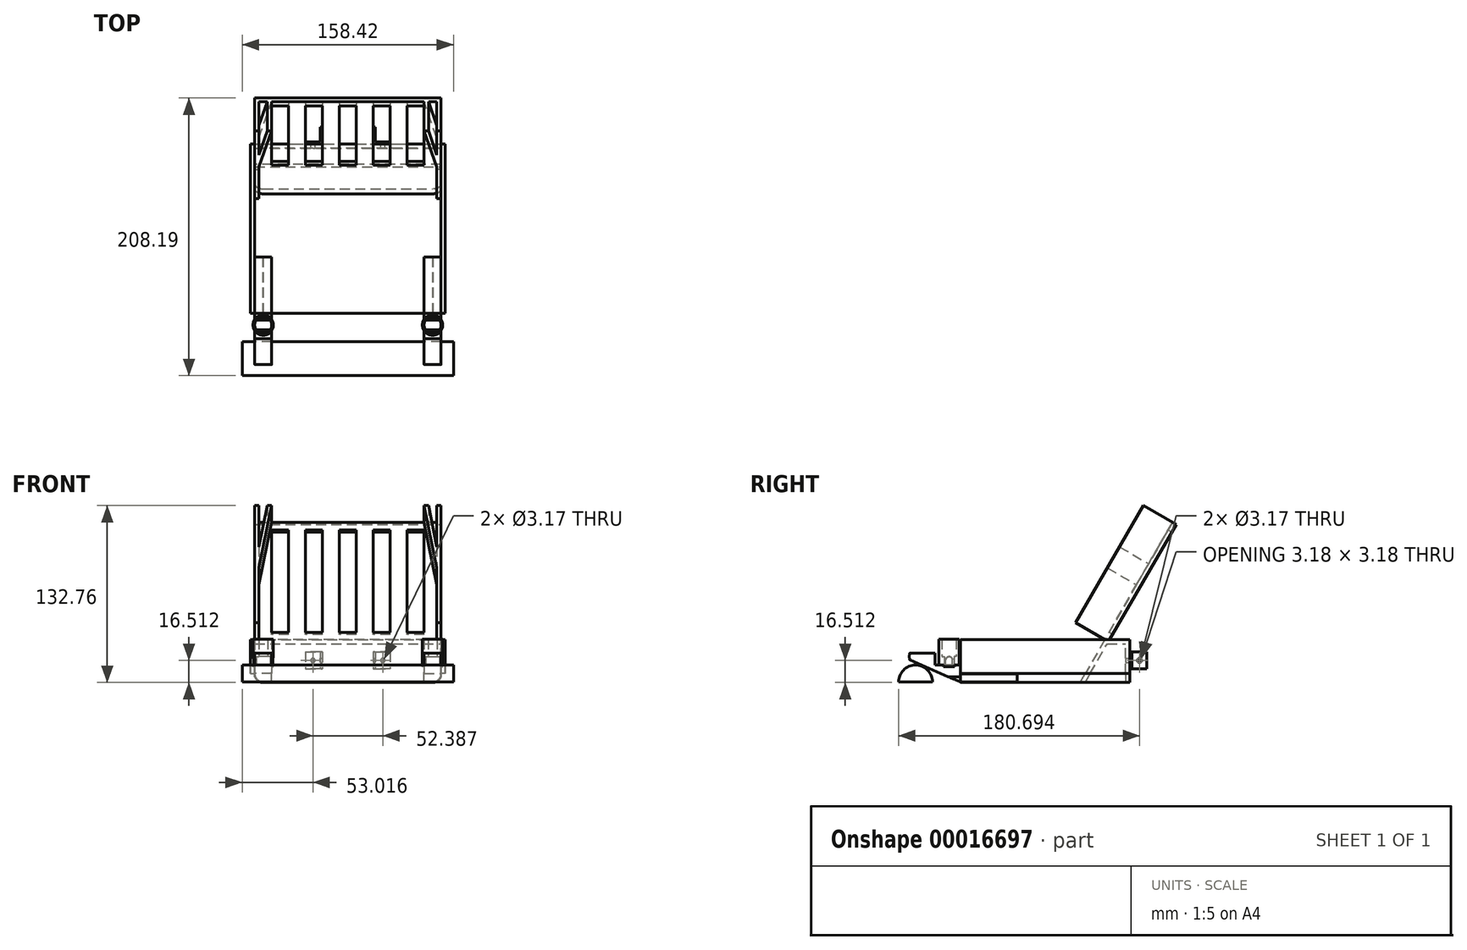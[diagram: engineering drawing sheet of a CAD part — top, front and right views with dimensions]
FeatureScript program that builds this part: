
annotation { "Feature Type Name" : "Feature", "Feature Type Description" : "" }
export const myFeature = defineFeature(function(context is Context, id is Id, definition is map)
    precondition{}
    {
        {
            var Q0;
            Q0=qCreatedBy(makeId("Front.planeOp"),FACE);
            var sketch = newSketch(context, id + "F0", { "sketchPlane" : qUnion([Q0])});
            skLineSegment(sketch, "E0.top", {"start": v(-63.5, 0) * mm, "end": v(63.5, 0) * mm});
            skLineSegment(sketch, "E0.left", {"start": v(-69.85, 31.75) * mm, "end": v(-69.85, 6.35) * mm});
            skLineSegment(sketch, "E0.right", {"start": v(69.85, 31.75) * mm, "end": v(69.85, 6.35) * mm});
            skLineSegment(sketch, "E1.0", {"start": v(70.17, 31.75) * mm, "end": v(70.17, 6.03) * mm});
            skLineSegment(sketch, "E1.1", {"start": v(-63.82, -0.32) * mm, "end": v(63.82, -0.32) * mm});
            skLineSegment(sketch, "E1.2", {"start": v(-70.17, 31.75) * mm, "end": v(-70.17, 6.03) * mm});
            skLineSegment(sketch, "E2", {"start": v(-70.17, 31.75) * mm, "end": v(-69.85, 31.75) * mm});
            skLineSegment(sketch, "E3", {"start": v(69.85, 31.75) * mm, "end": v(70.17, 31.75) * mm});
            skPoint(sketch, "E4.visualSharp", {"position": v(-70.17, -0.32) * mm});
            skArc(sketch, "E4.filletArc", {"start": v(-70.17, 6.03) * mm, "mid": v(-68.3, 1.54) * mm, "end": v(-63.82, -0.32) * mm});
            skPoint(sketch, "E5.visualSharp", {"position": v(-69.85, 0) * mm});
            skArc(sketch, "E5.filletArc", {"start": v(-69.85, 6.35) * mm, "mid": v(-68, 1.86) * mm, "end": v(-63.5, 0) * mm});
            skPoint(sketch, "E6.visualSharp", {"position": v(70.17, -0.32) * mm});
            skArc(sketch, "E6.filletArc", {"start": v(63.82, -0.32) * mm, "mid": v(68.3, 1.54) * mm, "end": v(70.17, 6.03) * mm});
            skPoint(sketch, "E7.visualSharp", {"position": v(69.85, 0) * mm});
            skArc(sketch, "E7.filletArc", {"start": v(63.5, 0) * mm, "mid": v(68, 1.86) * mm, "end": v(69.85, 6.35) * mm});
            skLineSegment(sketch, "E8.bottom", {"start": v(-70.17, 31.75) * mm, "end": v(-73.01, 31.75) * mm});
            skLineSegment(sketch, "E8.top", {"start": v(-70.17, 6.35) * mm, "end": v(-73.01, 6.35) * mm});
            skLineSegment(sketch, "E8.left", {"start": v(-70.17, 31.75) * mm, "end": v(-70.17, 6.35) * mm});
            skLineSegment(sketch, "E8.right", {"start": v(-73.01, 31.75) * mm, "end": v(-73.01, 6.35) * mm});
            skLineSegment(sketch, "E9", {"start": v(0, 0) * mm, "end": v(0, 50.9) * mm, "construction": true});
            skLineSegment(sketch, "E10.0.MirrorCS", {"start": v(70.17, 31.75) * mm, "end": v(73.01, 31.75) * mm});
            skLineSegment(sketch, "E11.0.MirrorCS", {"start": v(73.01, 31.75) * mm, "end": v(73.01, 6.35) * mm});
            skLineSegment(sketch, "E12.0.MirrorCS", {"start": v(70.17, 6.35) * mm, "end": v(73.01, 6.35) * mm});
            skSolve(sketch);
        }
        {
            var Q0;
            Q0=makeQuery(id+"F0.imprint","IMPRINT",FACE,{"disambiguationData":[TD([[makeQuery(id+"F0.imprint","IMPRINT",EDGE,{"derivedFrom":sQuery(id+"F0.wireOp",EDGE,"E0.top")}),-1.0]])]});
            extrude(context, id + "F1", {"entities" : qUnion([Q0]), "oppositeDirection" : true, "depth" : 127 * mm});
        }
        {
            var Q0;
            Q0=makeQuery(id+"F0.imprint","IMPRINT",FACE,{"disambiguationData":[TD([[makeQuery(id+"F0.imprint","IMPRINT",EDGE,{"derivedFrom":sQuery(id+"F0.wireOp",EDGE,"E8.bottom")}),1.0]])]});
            var Q1;
            {var subQ0=sQuery(id+"F0.wireOp",EDGE,"E10.0.MirrorCS");Q1=makeQuery(id+"F0.imprint","IMPRINT",FACE,{"disambiguationData":[TD([[makeQuery(id+"F0.imprint","IMPRINT",EDGE,{"derivedFrom":subQ0}),-1.0]])]});}
            var Q2;
            Q2=sQuery(id+"F0.wireOp",EDGE,"E8.right");
            var Q3;
            {var subQ0=sQuery(id+"F3.wireOp",EDGE,"E20.right");Q3=makeQuery(id+"F5.boolean.opBoolean","MERGE",FACE,{"derivedFrom":[makeQuery(id+"F4.boolean.opBoolean","MERGE",FACE,{"derivedFrom":[makeQuery(id+"F1.opExtrude","CAP_FACE",FACE,{"disambiguationData":[OSD([sQuery(id+"F0.wireOp",EDGE,"E0.top"),sQuery(id+"F0.wireOp",EDGE,"E0.left"),sQuery(id+"F0.wireOp",EDGE,"E0.right"),sQuery(id+"F0.wireOp",EDGE,"E1.0"),sQuery(id+"F0.wireOp",EDGE,"E1.1"),sQuery(id+"F0.wireOp",EDGE,"E1.2"),sQuery(id+"F0.wireOp",EDGE,"E2"),sQuery(id+"F0.wireOp",EDGE,"E3"),sQuery(id+"F0.wireOp",EDGE,"E4.filletArc"),sQuery(id+"F0.wireOp",EDGE,"E5.filletArc"),sQuery(id+"F0.wireOp",EDGE,"E6.filletArc"),sQuery(id+"F0.wireOp",EDGE,"E7.filletArc"),sQuery(id+"F0.wireOp",EDGE,"E8.left")])],"isStart":false}),makeQuery(id+"F4.opExtrude","SWEPT_FACE",FACE,{"disambiguationData":[OSD([subQ0])]})]}),makeQuery(id+"F5.opExtrude","SWEPT_FACE",FACE,{"disambiguationData":[OSD([subQ0])]})]});}
            extrude(context, id + "F2", {"entities" : qUnion([Q0, Q1]), "operationType" : NewBodyOperationType.ADD, "surfaceEntities" : qUnion([Q2]), "endBound" : BoundingType.UP_TO_SURFACE, "oppositeDirection" : true, "endBoundEntityFace" : qUnion([Q3]), "depth" : 25.4 * mm});
        }
        {
            var Q0;
            Q0=qCreatedBy(makeId("Right.planeOp"),FACE);
            var sketch = newSketch(context, id + "F3", { "sketchPlane" : qUnion([Q0])});
            skLineSegment(sketch, "E13", {"start": v(123.83, 31.75) * mm, "end": v(125.31, 31.75) * mm});
            skLineSegment(sketch, "E14", {"start": v(111.76, 31.75) * mm, "end": v(93.43, 0) * mm});
            skLineSegment(sketch, "E15", {"start": v(93.43, 0) * mm, "end": v(89.76, 0) * mm});
            skLineSegment(sketch, "E16", {"start": v(89.76, 0) * mm, "end": v(108.1, 31.75) * mm});
            skLineSegment(sketch, "E17", {"start": v(108.1, 31.75) * mm, "end": v(109.93, 31.75) * mm});
            skLineSegment(sketch, "E18.0", {"start": v(127, 6.35) * mm, "end": v(127, 6.03) * mm});
            skLineSegment(sketch, "E19.0", {"start": v(127, -0.32) * mm, "end": v(127, 6.03) * mm});
            skLineSegment(sketch, "E20.bottom", {"start": v(123.83, 31.75) * mm, "end": v(127, 31.75) * mm});
            skLineSegment(sketch, "E20.top", {"start": v(123.83, -0.32) * mm, "end": v(127, -0.32) * mm});
            skLineSegment(sketch, "E20.left", {"start": v(123.83, 31.75) * mm, "end": v(123.83, -0.32) * mm});
            skLineSegment(sketch, "E20.right", {"start": v(127, 31.75) * mm, "end": v(127, -0.32) * mm});
            skLineSegment(sketch, "E21.bottom", {"start": v(123.83, 31.75) * mm, "end": v(109.93, 31.75) * mm});
            skLineSegment(sketch, "E21.top", {"start": v(123.83, 28.58) * mm, "end": v(109.93, 28.58) * mm});
            skLineSegment(sketch, "E21.left", {"start": v(123.83, 31.75) * mm, "end": v(123.83, 28.58) * mm});
            skSolve(sketch);
        }
        {
            var Q0;
            Q0=qSketchRegion(id+"F3",true);
            var Q1;
            Q1=makeQuery(id+"F1.opExtrude","SWEPT_FACE",FACE,{"disambiguationData":[OSD([sQuery(id+"F0.wireOp",EDGE,"E1.2")])]});
            extrude(context, id + "F4", {"entities" : qUnion([Q0]), "operationType" : NewBodyOperationType.ADD, "endBound" : BoundingType.UP_TO_SURFACE, "oppositeDirection" : true, "endBoundEntityFace" : qUnion([Q1]), "depth" : 25.4 * mm});
        }
        {
            var Q0;
            Q0=qSketchRegion(id+"F3",true);
            var Q1;
            Q1=makeQuery(id+"F1.opExtrude","SWEPT_FACE",FACE,{"disambiguationData":[OSD([sQuery(id+"F0.wireOp",EDGE,"E1.0")])]});
            extrude(context, id + "F5", {"entities" : qUnion([Q0]), "operationType" : NewBodyOperationType.ADD, "endBound" : BoundingType.UP_TO_SURFACE, "endBoundEntityFace" : qUnion([Q1]), "depth" : 25.4 * mm});
        }
        {
            var Q0;
            Q0=qCreatedBy(makeId("Top.planeOp"),FACE);
            var sketch = newSketch(context, id + "F6", { "sketchPlane" : qUnion([Q0])});
            skLineSegment(sketch, "E22.bottom", {"start": v(-60.68, 0) * mm, "end": v(60.68, 0) * mm});
            skLineSegment(sketch, "E22.top", {"start": v(-60.68, -33.7) * mm, "end": v(60.68, -33.7) * mm});
            skLineSegment(sketch, "E22.left", {"start": v(-60.68, 0) * mm, "end": v(-60.68, -33.7) * mm});
            skLineSegment(sketch, "E22.right", {"start": v(60.68, 0) * mm, "end": v(60.68, -33.7) * mm});
            skSolve(sketch);
        }
        {
            var Q0;
            Q0=qSketchRegion(id+"F6",true);
            extrude(context, id + "F7", {"entities" : qUnion([Q0]), "operationType" : NewBodyOperationType.REMOVE, "endBound" : BoundingType.SYMMETRIC, "depth" : 25.4 * mm});
        }
        {
            var Q0;
            Q0=makeQuery(id+"FHrhu6zdTQCqyKD_1.boolean.opBoolean","MERGE",FACE,{"derivedFrom":[makeQuery(id+"F1.opExtrude","SWEPT_FACE",FACE,{"disambiguationData":[OSD([sQuery(id+"F0.wireOp",EDGE,"E1.1")])]}),makeQuery(id+"FHrhu6zdTQCqyKD_1.opExtrude","SWEPT_FACE",FACE,{"disambiguationData":[OSD([sQuery(id+"FeoMt1uyT1x2Saq_1.wireOp",EDGE,"f27479ac-693b-4c04-a3f3-3badf25c035c.1")])]})]});
            cPlane(context, id + "F8", {"entities" : qUnion([Q0]), "cplaneType" : CPlaneType.OFFSET, "offset" : 10.16 * mm, "oppositeDirection" : true, "width" : 152.4 * mm, "height" : 152.4 * mm});
        }
        {
            var Q0;
            Q0=qCreatedBy(id+"F8.planeOp",FACE);
            var sketch = newSketch(context, id + "F9", { "sketchPlane" : qUnion([Q0])});
            skLineSegment(sketch, "E23.0", {"start": v(-64.13, -127) * mm, "end": v(66.05, -127) * mm, "construction": true});
            skLineSegment(sketch, "E24", {"start": v(-31.75, -127) * mm, "end": v(-19.05, -127) * mm});
            skLineSegment(sketch, "E25", {"start": v(-19.05, -127) * mm, "end": v(-19.05, -139.7) * mm});
            skLineSegment(sketch, "E26", {"start": v(-19.05, -139.7) * mm, "end": v(-20.64, -139.7) * mm});
            skLineSegment(sketch, "E27", {"start": v(-20.64, -139.7) * mm, "end": v(-20.64, -128.59) * mm});
            skLineSegment(sketch, "E28", {"start": v(-20.64, -128.59) * mm, "end": v(-31.75, -128.59) * mm});
            skLineSegment(sketch, "E29", {"start": v(-31.75, -127) * mm, "end": v(-31.75, -128.59) * mm});
            skPoint(sketch, "E30", {"position": v(0, -127) * mm});
            skLineSegment(sketch, "E31", {"start": v(0, -127) * mm, "end": v(0, -64.75) * mm, "construction": true});
            skLineSegment(sketch, "E32.0.MirrorCS", {"start": v(19.05, -139.7) * mm, "end": v(20.64, -139.7) * mm});
            skLineSegment(sketch, "E32.1.MirrorCS", {"start": v(31.75, -127) * mm, "end": v(31.75, -128.59) * mm});
            skLineSegment(sketch, "E32.2.MirrorCS", {"start": v(31.75, -127) * mm, "end": v(19.05, -127) * mm});
            skLineSegment(sketch, "E32.3.MirrorCS", {"start": v(20.64, -139.7) * mm, "end": v(20.64, -128.59) * mm});
            skLineSegment(sketch, "E32.4.MirrorCS", {"start": v(20.64, -128.59) * mm, "end": v(31.75, -128.59) * mm});
            skLineSegment(sketch, "E32.5.MirrorCS", {"start": v(19.05, -127) * mm, "end": v(19.05, -139.7) * mm});
            skSolve(sketch);
        }
        {
            var Q0;
            Q0=qSketchRegion(id+"F9",true);
            extrude(context, id + "F10", {"entities" : qUnion([Q0]), "operationType" : NewBodyOperationType.ADD, "oppositeDirection" : true, "depth" : 12.7 * mm});
        }
        {
            var Q0;
            Q0=makeQuery(id+"F10.opExtrude","SWEPT_FACE",FACE,{"disambiguationData":[OSD([sQuery(id+"F9.wireOp",EDGE,"E32.3.MirrorCS")])]});
            var sketch = newSketch(context, id + "F11", { "sketchPlane" : qUnion([Q0])});
            skPoint(sketch, "E33", {"position": v(134.14, 22.54) * mm});
            skPoint(sketch, "E34", {"position": v(139.7, 16.2) * mm});
            skCircle(sketch, "E35", {"center": v(134.14, 16.2) * mm, "radius": 1.59 * mm});
            skSolve(sketch);
        }
        {
            var Q0;
            Q0=qSketchRegion(id+"F11",true);
            extrude(context, id + "F12", {"entities" : qUnion([Q0]), "operationType" : NewBodyOperationType.REMOVE, "endBound" : BoundingType.THROUGH_ALL, "oppositeDirection" : true, "depth" : 25.4 * mm});
        }
        {
            var Q0;
            Q0=makeQuery(id+"F10.opExtrude","SWEPT_FACE",FACE,{"disambiguationData":[OSD([sQuery(id+"F9.wireOp",EDGE,"E32.4.MirrorCS")])]});
            var sketch = newSketch(context, id + "F13", { "sketchPlane" : qUnion([Q0])});
            skPoint(sketch, "E36", {"position": v(-26.2, 22.54) * mm});
            skPoint(sketch, "E37", {"position": v(-31.75, 16.2) * mm});
            skPoint(sketch, "E38", {"position": v(0, 35.4) * mm});
            skPoint(sketch, "E39", {"position": v(0, 0) * mm});
            skLineSegment(sketch, "E40", {"start": v(0, 35.4) * mm, "end": v(0, 0) * mm, "construction": true});
            skPoint(sketch, "E41.0.MirrorP", {"position": v(26.2, 22.54) * mm});
            skCircle(sketch, "E42", {"center": v(-26.2, 16.2) * mm, "radius": 1.59 * mm});
            skCircle(sketch, "E43", {"center": v(26.2, 16.2) * mm, "radius": 1.59 * mm});
            skSolve(sketch);
        }
        {
            var Q0;
            Q0=qSketchRegion(id+"F13",true);
            var Q1;
            Q1=makeQuery(id+"F4.opExtrude","SWEPT_FACE",FACE,{"disambiguationData":[OSD([sQuery(id+"F3.wireOp",EDGE,"05d0a0fc-6501-4c31-99f1-73c3115c6615")])]});
            extrude(context, id + "F14", {"entities" : qUnion([Q0]), "operationType" : NewBodyOperationType.REMOVE, "oppositeDirection" : true, "endBoundEntity" : qUnion([Q1]), "depth" : 6.35 * mm});
        }
        {
            var Q0;
            {var subQ0=sQuery(id+"F3.wireOp",EDGE,"E16");Q0=makeQuery(id+"F5.boolean.opBoolean","MERGE",FACE,{"derivedFrom":[makeQuery(id+"F4.boolean.opBoolean","SPLIT",FACE,{"disambiguationData":[TD([makeQuery(id+"F1.opExtrude","SWEPT_FACE",FACE,{"disambiguationData":[OSD([sQuery(id+"F0.wireOp",EDGE,"E0.top")])]})])],"derivedFrom":makeQuery(id+"F4.opExtrude","SWEPT_FACE",FACE,{"disambiguationData":[OSD([subQ0])]})}),makeQuery(id+"F5.opExtrude","SWEPT_FACE",FACE,{"disambiguationData":[OSD([subQ0])]})]});}
            var sketch = newSketch(context, id + "F15", { "sketchPlane" : qUnion([Q0])});
            skLineSegment(sketch, "E44.0.0", {"start": v(-69.85, 81.54) * mm, "end": v(-69.85, 52.21) * mm});
            skFitSpline(sketch, "E44.0.1", {"points": [v(-63.5, 44.88) * mm, v(1000, -50.8) * mm, v(44.88, 333.33) * mm, v(-50.8, 59.55) * mm, v(333.33, -63.5) * mm, v(59.55, 1000) * mm, v(-76.2, 59.55) * mm]});
            skLineSegment(sketch, "E44.0.2", {"start": v(-63.5, 44.88) * mm, "end": v(63.5, 44.88) * mm});
            skFitSpline(sketch, "E44.0.3", {"points": [v(63.5, 44.88) * mm, v(1000, 50.8) * mm, v(44.88, 333.33) * mm, v(50.8, 59.55) * mm, v(333.33, 63.5) * mm, v(59.55, 1000) * mm, v(76.2, 59.55) * mm]});
            skLineSegment(sketch, "E44.0.4", {"start": v(69.85, 52.21) * mm, "end": v(69.85, 81.54) * mm});
            skLineSegment(sketch, "E44.0.5", {"start": v(-69.85, 81.54) * mm, "end": v(69.85, 81.54) * mm});
            skLineSegment(sketch, "E45", {"start": v(-69.85, 81.54) * mm, "end": v(-69.85, 183.14) * mm});
            skLineSegment(sketch, "E46", {"start": v(-69.85, 183.14) * mm, "end": v(69.85, 183.14) * mm});
            skLineSegment(sketch, "E47", {"start": v(69.85, 183.14) * mm, "end": v(69.85, 81.54) * mm});
            skLineSegment(sketch, "E48.bottom", {"start": v(57.15, 88.02) * mm, "end": v(44.45, 88.02) * mm});
            skLineSegment(sketch, "E48.top", {"start": v(57.15, 176.48) * mm, "end": v(44.45, 176.48) * mm});
            skLineSegment(sketch, "E48.left", {"start": v(57.15, 88.02) * mm, "end": v(57.15, 176.48) * mm});
            skLineSegment(sketch, "E48.right", {"start": v(44.45, 88.02) * mm, "end": v(44.45, 176.48) * mm});
            skLineSegment(sketch, "E49.1.0.0", {"start": v(19.05, 88.02) * mm, "end": v(19.05, 176.48) * mm});
            skLineSegment(sketch, "E49.1.0.1", {"start": v(31.75, 88.02) * mm, "end": v(19.05, 88.02) * mm});
            skLineSegment(sketch, "E49.1.0.2", {"start": v(31.75, 88.02) * mm, "end": v(31.75, 176.48) * mm});
            skLineSegment(sketch, "E49.1.0.3", {"start": v(31.75, 176.48) * mm, "end": v(19.05, 176.48) * mm});
            skLineSegment(sketch, "E49.2.0.0", {"start": v(-6.35, 88.02) * mm, "end": v(-6.35, 176.48) * mm});
            skLineSegment(sketch, "E49.2.0.1", {"start": v(6.35, 88.02) * mm, "end": v(-6.35, 88.02) * mm});
            skLineSegment(sketch, "E49.2.0.2", {"start": v(6.35, 88.02) * mm, "end": v(6.35, 176.48) * mm});
            skLineSegment(sketch, "E49.2.0.3", {"start": v(6.35, 176.48) * mm, "end": v(-6.35, 176.48) * mm});
            skLineSegment(sketch, "E49.direction1", {"start": v(44.45, 88.02) * mm, "end": v(19.05, 88.02) * mm, "construction": true});
            skLineSegment(sketch, "E50.0.3.0", {"start": v(-31.75, 88.02) * mm, "end": v(-31.75, 176.48) * mm});
            skLineSegment(sketch, "E50.3.3.0", {"start": v(-19.05, 88.02) * mm, "end": v(-31.75, 88.02) * mm});
            skLineSegment(sketch, "E50.6.3.0", {"start": v(-19.05, 88.02) * mm, "end": v(-19.05, 176.48) * mm});
            skLineSegment(sketch, "E50.9.3.0", {"start": v(-19.05, 176.48) * mm, "end": v(-31.75, 176.48) * mm});
            skLineSegment(sketch, "E51.0.4.0", {"start": v(-57.15, 88.02) * mm, "end": v(-57.15, 176.48) * mm});
            skLineSegment(sketch, "E51.3.4.0", {"start": v(-44.45, 88.02) * mm, "end": v(-57.15, 88.02) * mm});
            skLineSegment(sketch, "E51.6.4.0", {"start": v(-44.45, 88.02) * mm, "end": v(-44.45, 176.48) * mm});
            skLineSegment(sketch, "E51.9.4.0", {"start": v(-44.45, 176.48) * mm, "end": v(-57.15, 176.48) * mm});
            skLineSegment(sketch, "E52.bottom", {"start": v(-69.85, 176.8) * mm, "end": v(-66.67, 176.8) * mm});
            skLineSegment(sketch, "E52.top", {"start": v(-69.85, 164.1) * mm, "end": v(-66.67, 164.1) * mm});
            skLineSegment(sketch, "E52.left", {"start": v(-69.85, 176.8) * mm, "end": v(-69.85, 164.1) * mm});
            skLineSegment(sketch, "E52.right", {"start": v(-66.67, 176.8) * mm, "end": v(-66.67, 164.1) * mm});
            skLineSegment(sketch, "E53", {"start": v(0, 81.54) * mm, "end": v(0, 183.14) * mm, "construction": true});
            skLineSegment(sketch, "E54.1.0.0", {"start": v(-66.67, 138.7) * mm, "end": v(-66.67, 126) * mm});
            skLineSegment(sketch, "E54.1.0.1", {"start": v(-69.85, 138.7) * mm, "end": v(-66.67, 138.7) * mm});
            skLineSegment(sketch, "E54.1.0.2", {"start": v(-69.85, 126) * mm, "end": v(-66.67, 126) * mm});
            skLineSegment(sketch, "E54.2.0.0", {"start": v(-66.67, 100.6) * mm, "end": v(-66.67, 87.9) * mm});
            skLineSegment(sketch, "E54.2.0.1", {"start": v(-69.85, 100.6) * mm, "end": v(-66.67, 100.6) * mm});
            skLineSegment(sketch, "E54.2.0.2", {"start": v(-69.85, 87.9) * mm, "end": v(-66.67, 87.9) * mm});
            skLineSegment(sketch, "E54.direction1", {"start": v(-66.67, 164.1) * mm, "end": v(-66.67, 126) * mm, "construction": true});
            skLineSegment(sketch, "E55.0.MirrorCS", {"start": v(66.68, 176.8) * mm, "end": v(66.68, 164.1) * mm});
            skLineSegment(sketch, "E56.0.MirrorCS", {"start": v(69.85, 164.1) * mm, "end": v(66.68, 164.1) * mm});
            skLineSegment(sketch, "E57.0.MirrorCS", {"start": v(69.85, 176.8) * mm, "end": v(66.68, 176.8) * mm});
            skLineSegment(sketch, "E58.0.MirrorCS", {"start": v(69.85, 138.7) * mm, "end": v(66.68, 138.7) * mm});
            skLineSegment(sketch, "E59.0.MirrorCS", {"start": v(66.68, 138.7) * mm, "end": v(66.68, 126) * mm});
            skLineSegment(sketch, "E60.0.MirrorCS", {"start": v(69.85, 126) * mm, "end": v(66.67, 126) * mm});
            skLineSegment(sketch, "E61.0.MirrorCS", {"start": v(69.85, 100.6) * mm, "end": v(66.67, 100.6) * mm});
            skLineSegment(sketch, "E62.0.MirrorCS", {"start": v(66.67, 100.6) * mm, "end": v(66.67, 87.9) * mm});
            skLineSegment(sketch, "E63.0.MirrorCS", {"start": v(69.85, 87.9) * mm, "end": v(66.67, 87.9) * mm});
            skSolve(sketch);
        }
        {
            var Q0;
            Q0=makeQuery(id+"F15.imprint","IMPRINT",FACE,{"disambiguationData":[TD([[makeQuery(id+"F15.imprint","IMPRINT",EDGE,{"derivedFrom":sQuery(id+"F15.wireOp",EDGE,"E44.0.5")}),1.0]])]});
            extrude(context, id + "F16", {"entities" : qUnion([Q0]), "operationType" : NewBodyOperationType.ADD, "oppositeDirection" : true, "depth" : 3.17 * mm});
        }
        {
            var Q0;
            {var subQ0=sQuery(id+"F0.wireOp",EDGE,"E0.left");var subQ2=sQuery(id+"F0.wireOp",EDGE,"E2");Q0=makeQuery(id+"F4.boolean.opBoolean","SPLIT",FACE,{"disambiguationData":[TD([makeQuery(id+"F1.opExtrude","SWEPT_FACE",FACE,{"disambiguationData":[OSD([subQ2])]})])],"derivedFrom":makeQuery(id+"F1.opExtrude","SWEPT_FACE",FACE,{"disambiguationData":[OSD([subQ0])]})});}
            var sketch = newSketch(context, id + "F17", { "sketchPlane" : qUnion([Q0])});
            skLineSegment(sketch, "E64.0.1", {"start": v(125.31, 31.75) * mm, "end": v(0, 31.75) * mm, "construction": true});
            skLineSegment(sketch, "E64.0.2", {"start": v(0, 31.75) * mm, "end": v(0, 6.35) * mm, "construction": true});
            skLineSegment(sketch, "E65.top", {"start": v(42.38, 12.7) * mm, "end": v(0, 12.7) * mm});
            skLineSegment(sketch, "E65.left", {"start": v(42.38, 0) * mm, "end": v(42.38, 12.7) * mm});
            skLineSegment(sketch, "E65.right", {"start": v(0, 0) * mm, "end": v(0, 12.7) * mm});
            skLineSegment(sketch, "E66", {"start": v(0, 6.35) * mm, "end": v(-29.37, 6.35) * mm, "construction": true});
            skArc(sketch, "E67", {"start": v(-38.25, 21.59) * mm, "mid": v(-23.52, 0.2) * mm, "end": v(-0.75, 12.7) * mm});
            skPoint(sketch, "E68", {"position": v(-19.05, -0.32) * mm});
            skLineSegment(sketch, "E69", {"start": v(0, 12.7) * mm, "end": v(-0.75, 12.7) * mm});
            skLineSegment(sketch, "E70", {"start": v(0, -0.32) * mm, "end": v(-19.05, -0.32) * mm});
            skLineSegment(sketch, "E71", {"start": v(42.38, 0) * mm, "end": v(0, 0) * mm});
            skLineSegment(sketch, "E72", {"start": v(0, 0) * mm, "end": v(0, -0.32) * mm});
            skLineSegment(sketch, "E73", {"start": v(-19.05, 21.59) * mm, "end": v(-19.05, 12.7) * mm});
            skLineSegment(sketch, "E74", {"start": v(-19.05, 12.7) * mm, "end": v(-0.75, 12.7) * mm});
            skLineSegment(sketch, "E75.trimOffspring", {"start": v(-19.05, 21.59) * mm, "end": v(-38.25, 21.59) * mm});
            skLineSegment(sketch, "E76", {"start": v(0, 0) * mm, "end": v(-38.27, 16.7) * mm});
            skSolve(sketch);
        }
        {
            var Q0;
            Q0=makeQuery(id+"F17.imprint","IMPRINT",FACE,{"disambiguationData":[TD([[makeQuery(id+"F17.imprint","IMPRINT",EDGE,{"derivedFrom":sQuery(id+"F17.wireOp",EDGE,"E73")}),-1.0]])]});
            var Q1;
            {var subQ5=sQuery(id+"F17.wireOp",EDGE,"E69");Q1=makeQuery(id+"F17.imprint","IMPRINT",FACE,{"disambiguationData":[TD([[makeQuery(id+"F17.imprint","IMPRINT",EDGE,{"derivedFrom":subQ5}),1.0]])]});}
            var Q2;
            {var subQ9=sQuery(id+"F17.wireOp",EDGE,"E71");Q2=makeQuery(id+"F17.imprint","IMPRINT",FACE,{"disambiguationData":[TD([[makeQuery(id+"F17.imprint","IMPRINT",EDGE,{"derivedFrom":subQ9}),-1.0]])]});}
            extrude(context, id + "F18", {"entities" : qUnion([Q0, Q1, Q2]), "depth" : 12.7 * mm});
        }
        {
            var Q0;
            Q0=makeQuery(id+"F1.opExtrude","CAP_FACE",FACE,{"disambiguationData":[OSD([sQuery(id+"F0.wireOp",EDGE,"E0.top"),sQuery(id+"F0.wireOp",EDGE,"E0.left"),sQuery(id+"F0.wireOp",EDGE,"E0.right"),sQuery(id+"F0.wireOp",EDGE,"E1.0"),sQuery(id+"F0.wireOp",EDGE,"E1.1"),sQuery(id+"F0.wireOp",EDGE,"E1.2"),sQuery(id+"F0.wireOp",EDGE,"E2"),sQuery(id+"F0.wireOp",EDGE,"E3"),sQuery(id+"F0.wireOp",EDGE,"E4.filletArc"),sQuery(id+"F0.wireOp",EDGE,"E5.filletArc"),sQuery(id+"F0.wireOp",EDGE,"E6.filletArc"),sQuery(id+"F0.wireOp",EDGE,"E7.filletArc")])],"isStart":true});
            var sketch = newSketch(context, id + "F19", { "sketchPlane" : qUnion([Q0])});
            skArc(sketch, "E77.0", {"start": v(-70.17, 6.03) * mm, "mid": v(-68.3, 1.54) * mm, "end": v(-63.82, -0.32) * mm});
            skLineSegment(sketch, "E78", {"start": v(-70.17, 6.03) * mm, "end": v(-70.17, -0.32) * mm});
            skLineSegment(sketch, "E79", {"start": v(-63.82, -0.32) * mm, "end": v(-70.17, -0.32) * mm});
            skArc(sketch, "E80.0", {"start": v(-69.85, 6.35) * mm, "mid": v(-68, 1.86) * mm, "end": v(-63.5, 0) * mm});
            skLineSegment(sketch, "E81", {"start": v(-69.85, 6.35) * mm, "end": v(-70.17, 6.03) * mm});
            skLineSegment(sketch, "E82", {"start": v(-63.5, 0) * mm, "end": v(-63.82, -0.32) * mm});
            skLineSegment(sketch, "E83.0.MirrorCS", {"start": v(69.85, 6.35) * mm, "end": v(70.17, 6.03) * mm});
            skLineSegment(sketch, "E83.1.MirrorCS", {"start": v(63.5, 0) * mm, "end": v(63.82, -0.32) * mm});
            skLineSegment(sketch, "E83.2.MirrorCS", {"start": v(63.82, -0.32) * mm, "end": v(70.17, -0.32) * mm});
            skArc(sketch, "E83.3.MirrorCS", {"start": v(69.85, 6.35) * mm, "mid": v(68, 1.86) * mm, "end": v(63.5, 0) * mm});
            skLineSegment(sketch, "E83.4.MirrorCS", {"start": v(70.17, 6.03) * mm, "end": v(70.17, -0.32) * mm});
            skArc(sketch, "E83.5.MirrorCS", {"start": v(70.17, 6.03) * mm, "mid": v(68.3, 1.54) * mm, "end": v(63.82, -0.32) * mm});
            skSolve(sketch);
        }
        {
            var Q0;
            Q0=makeQuery(id+"F19.imprint","IMPRINT",FACE,{"disambiguationData":[TD([[makeQuery(id+"F19.imprint","IMPRINT",EDGE,{"derivedFrom":sQuery(id+"F19.wireOp",EDGE,"E77.0")}),-1.0]])]});
            var Q1;
            Q1=sQuery(id+"F19.wireOp",EDGE,"E78");
            var Q2;
            Q2=sQuery(id+"F19.wireOp",EDGE,"E77.0");
            var Q3;
            Q3=sQuery(id+"F19.wireOp",EDGE,"E79");
            var Q4;
            Q4=makeQuery(id+"F1.opExtrude","CAP_FACE",FACE,{"disambiguationData":[OSD([sQuery(id+"F0.wireOp",EDGE,"E0.top"),sQuery(id+"F0.wireOp",EDGE,"E0.left"),sQuery(id+"F0.wireOp",EDGE,"E0.right"),sQuery(id+"F0.wireOp",EDGE,"E1.0"),sQuery(id+"F0.wireOp",EDGE,"E1.1"),sQuery(id+"F0.wireOp",EDGE,"E1.2"),sQuery(id+"F0.wireOp",EDGE,"E2"),sQuery(id+"F0.wireOp",EDGE,"E3"),sQuery(id+"F0.wireOp",EDGE,"E4.filletArc"),sQuery(id+"F0.wireOp",EDGE,"E5.filletArc"),sQuery(id+"F0.wireOp",EDGE,"E6.filletArc"),sQuery(id+"F0.wireOp",EDGE,"E7.filletArc")])],"isStart":true});
            extrude(context, id + "F20", {"entities" : qUnion([Q0]), "operationType" : NewBodyOperationType.REMOVE, "surfaceEntities" : qUnion([Q1, Q2, Q3]), "endBound" : BoundingType.UP_TO_NEXT, "endBoundEntity" : qUnion([Q4]), "depth" : 25.4 * mm});
        }
        {
            var Q0;
            Q0=qSketchRegion(id+"F19",true);
            var Q1;
            Q1=makeQuery(id+"F18.opExtrude","SWEPT_FACE",FACE,{"disambiguationData":[OSD([sQuery(id+"F17.wireOp",EDGE,"E65.left")])]});
            extrude(context, id + "F21", {"entities" : qUnion([Q0]), "operationType" : NewBodyOperationType.REMOVE, "endBound" : BoundingType.UP_TO_SURFACE, "oppositeDirection" : true, "endBoundEntityFace" : qUnion([Q1]), "depth" : 25.4 * mm});
        }
        {
            var Q0;
            Q0=makeQuery(id+"F18.opExtrude","SWEPT_FACE",FACE,{"disambiguationData":[OSD([sQuery(id+"F17.wireOp",EDGE,"E67")])]});
            fillet(context, id + "F22", {"entities" : qUnion([Q0]), "radius" : 0.25 * mm, "tangentPropagation" : true, "allowEdgeOverflow" : false});
        }
        {
            var Q0;
            Q0=makeQuery(id+"F18.opExtrude","SWEPT_FACE",FACE,{"disambiguationData":[OSD([sQuery(id+"F17.wireOp",EDGE,"E65.top"),sQuery(id+"F17.wireOp",EDGE,"E69")])]});
            var sketch = newSketch(context, id + "F23", { "sketchPlane" : qUnion([Q0])});
            skCircle(sketch, "E84", {"center": v(-63.5, -8.65) * mm, "radius": 7.62 * mm});
            skCircle(sketch, "E85", {"center": v(-63.5, -8.65) * mm, "radius": 6.35 * mm});
            skLineSegment(sketch, "E86", {"start": v(-66.89, -3.28) * mm, "end": v(-60.11, -3.28) * mm});
            skLineSegment(sketch, "E87", {"start": v(-66.89, -14.02) * mm, "end": v(-60.11, -14.02) * mm});
            skCircle(sketch, "E88", {"center": v(-63.5, -8.65) * mm, "radius": 5.37 * mm, "construction": true});
            skLineSegment(sketch, "E89", {"start": v(-57.15, -8.65) * mm, "end": v(-69.85, -8.65) * mm});
            skCircle(sketch, "E90", {"center": v(-63.5, -8.65) * mm, "radius": 3.6 * mm, "construction": true});
            skLineSegment(sketch, "E91", {"start": v(-58.26, -12.24) * mm, "end": v(-68.74, -12.24) * mm});
            skLineSegment(sketch, "E92", {"start": v(-58.26, -5.06) * mm, "end": v(-68.74, -5.06) * mm});
            skSolve(sketch);
        }
        {
            var Q0;
            {var subQ5=sQuery(id+"F23.wireOp",EDGE,"E85");var subQ11=sQuery(id+"F23.wireOp",EDGE,"E86");var subQ13=makeQuery(id+"F23.imprint","INTERSECT",VERTEX,{"disambiguationData":[OD(0.0)],"derivedFrom":[subQ5,subQ11]});Q0=makeQuery(id+"F23.imprint","IMPRINT",FACE,{"disambiguationData":[TD([[makeQuery(id+"F23.imprint","IMPRINT",EDGE,{"disambiguationData":[TD([[subQ13,-1.0]])],"derivedFrom":subQ5}),-1.0]])]});}
            var Q1;
            {var subQ0=makeQuery(id+"F18.opExtrude","CAP_EDGE",EDGE,{"disambiguationData":[OSD([sQuery(id+"F17.wireOp",EDGE,"E69"),sQuery(id+"F17.wireOp",EDGE,"E74")])],"isStart":true});var subQ1=sQuery(id+"F23.wireOp",EDGE,"E84");var subQ4=makeQuery(id+"F23.imprint","INTERSECT",VERTEX,{"disambiguationData":[OD(0.0)],"derivedFrom":[subQ0,subQ1]});Q1=makeQuery(id+"F23.imprint","IMPRINT",FACE,{"disambiguationData":[TD([[makeQuery(id+"F23.imprint","IMPRINT",EDGE,{"disambiguationData":[TD([[subQ4,-1.0]])],"derivedFrom":subQ1}),1.0]])]});}
            var Q2;
            {var subQ5=sQuery(id+"F23.wireOp",EDGE,"E85");var subQ13=sQuery(id+"F23.wireOp",EDGE,"E87");var subQ15=makeQuery(id+"F23.imprint","INTERSECT",VERTEX,{"disambiguationData":[OD(0.0)],"derivedFrom":[subQ5,subQ13]});Q2=makeQuery(id+"F23.imprint","IMPRINT",FACE,{"disambiguationData":[TD([[makeQuery(id+"F23.imprint","IMPRINT",EDGE,{"disambiguationData":[TD([[subQ15,1.0]])],"derivedFrom":subQ5}),-1.0]])]});}
            var Q3;
            {var subQ0=makeQuery(id+"F18.opExtrude","CAP_EDGE",EDGE,{"disambiguationData":[OSD([sQuery(id+"F17.wireOp",EDGE,"E69"),sQuery(id+"F17.wireOp",EDGE,"E74")])],"isStart":false});var subQ1=sQuery(id+"F23.wireOp",EDGE,"E84");var subQ4=makeQuery(id+"F23.imprint","INTERSECT",VERTEX,{"disambiguationData":[OD(0.0)],"derivedFrom":[subQ0,subQ1]});Q3=makeQuery(id+"F23.imprint","IMPRINT",FACE,{"disambiguationData":[TD([[makeQuery(id+"F23.imprint","IMPRINT",EDGE,{"disambiguationData":[TD([[subQ4,1.0]])],"derivedFrom":subQ1}),1.0]])]});}
            var Q4;
            {var subQ0=sQuery(id+"F23.wireOp",EDGE,"E87");Q4=makeQuery(id+"F23.imprint","IMPRINT",FACE,{"disambiguationData":[TD([[makeQuery(id+"F23.imprint","IMPRINT",EDGE,{"derivedFrom":subQ0}),-1.0]])]});}
            var Q5;
            {var subQ1=sQuery(id+"F23.wireOp",EDGE,"E87");Q5=makeQuery(id+"F23.imprint","IMPRINT",FACE,{"disambiguationData":[TD([[makeQuery(id+"F23.imprint","IMPRINT",EDGE,{"derivedFrom":subQ1}),1.0]])]});}
            var Q6;
            {var subQ1=sQuery(id+"F23.wireOp",EDGE,"E86");Q6=makeQuery(id+"F23.imprint","IMPRINT",FACE,{"disambiguationData":[TD([[makeQuery(id+"F23.imprint","IMPRINT",EDGE,{"derivedFrom":subQ1}),-1.0]])]});}
            var Q7;
            {var subQ0=sQuery(id+"F23.wireOp",EDGE,"E86");Q7=makeQuery(id+"F23.imprint","IMPRINT",FACE,{"disambiguationData":[TD([[makeQuery(id+"F23.imprint","IMPRINT",EDGE,{"derivedFrom":subQ0}),1.0]])]});}
            extrude(context, id + "F24", {"entities" : qUnion([Q0, Q1, Q2, Q3, Q4, Q5, Q6, Q7]), "operationType" : NewBodyOperationType.ADD, "oppositeDirection" : true, "depth" : 1.27 * mm});
        }
        {
            var Q0;
            {var subQ5=sQuery(id+"F23.wireOp",EDGE,"E85");var subQ11=sQuery(id+"F23.wireOp",EDGE,"E86");var subQ13=makeQuery(id+"F23.imprint","INTERSECT",VERTEX,{"disambiguationData":[OD(0.0)],"derivedFrom":[subQ5,subQ11]});Q0=makeQuery(id+"F23.imprint","IMPRINT",FACE,{"disambiguationData":[TD([[makeQuery(id+"F23.imprint","IMPRINT",EDGE,{"disambiguationData":[TD([[subQ13,-1.0]])],"derivedFrom":subQ5}),-1.0]])]});}
            var Q1;
            {var subQ5=sQuery(id+"F23.wireOp",EDGE,"E85");var subQ13=sQuery(id+"F23.wireOp",EDGE,"E87");var subQ15=makeQuery(id+"F23.imprint","INTERSECT",VERTEX,{"disambiguationData":[OD(0.0)],"derivedFrom":[subQ5,subQ13]});Q1=makeQuery(id+"F23.imprint","IMPRINT",FACE,{"disambiguationData":[TD([[makeQuery(id+"F23.imprint","IMPRINT",EDGE,{"disambiguationData":[TD([[subQ15,1.0]])],"derivedFrom":subQ5}),-1.0]])]});}
            var Q2;
            {var subQ0=makeQuery(id+"F18.opExtrude","CAP_EDGE",EDGE,{"disambiguationData":[OSD([sQuery(id+"F17.wireOp",EDGE,"E69"),sQuery(id+"F17.wireOp",EDGE,"E74")])],"isStart":false});var subQ1=sQuery(id+"F23.wireOp",EDGE,"E84");var subQ4=makeQuery(id+"F23.imprint","INTERSECT",VERTEX,{"disambiguationData":[OD(0.0)],"derivedFrom":[subQ0,subQ1]});Q2=makeQuery(id+"F23.imprint","IMPRINT",FACE,{"disambiguationData":[TD([[makeQuery(id+"F23.imprint","IMPRINT",EDGE,{"disambiguationData":[TD([[subQ4,1.0]])],"derivedFrom":subQ1}),1.0]])]});}
            var Q3;
            {var subQ0=makeQuery(id+"F18.opExtrude","CAP_EDGE",EDGE,{"disambiguationData":[OSD([sQuery(id+"F17.wireOp",EDGE,"E69"),sQuery(id+"F17.wireOp",EDGE,"E74")])],"isStart":true});var subQ1=sQuery(id+"F23.wireOp",EDGE,"E84");var subQ4=makeQuery(id+"F23.imprint","INTERSECT",VERTEX,{"disambiguationData":[OD(0.0)],"derivedFrom":[subQ0,subQ1]});Q3=makeQuery(id+"F23.imprint","IMPRINT",FACE,{"disambiguationData":[TD([[makeQuery(id+"F23.imprint","IMPRINT",EDGE,{"disambiguationData":[TD([[subQ4,-1.0]])],"derivedFrom":subQ1}),1.0]])]});}
            var Q4;
            {var subQ1=sQuery(id+"F23.wireOp",EDGE,"E87");Q4=makeQuery(id+"F23.imprint","IMPRINT",FACE,{"disambiguationData":[TD([[makeQuery(id+"F23.imprint","IMPRINT",EDGE,{"derivedFrom":subQ1}),1.0]])]});}
            var Q5;
            {var subQ1=sQuery(id+"F23.wireOp",EDGE,"E86");Q5=makeQuery(id+"F23.imprint","IMPRINT",FACE,{"disambiguationData":[TD([[makeQuery(id+"F23.imprint","IMPRINT",EDGE,{"derivedFrom":subQ1}),-1.0]])]});}
            var Q6;
            {var subQ0=sQuery(id+"F23.wireOp",EDGE,"E87");Q6=makeQuery(id+"F23.imprint","IMPRINT",FACE,{"disambiguationData":[TD([[makeQuery(id+"F23.imprint","IMPRINT",EDGE,{"derivedFrom":subQ0}),-1.0]])]});}
            var Q7;
            {var subQ0=sQuery(id+"F23.wireOp",EDGE,"E86");Q7=makeQuery(id+"F23.imprint","IMPRINT",FACE,{"disambiguationData":[TD([[makeQuery(id+"F23.imprint","IMPRINT",EDGE,{"derivedFrom":subQ0}),1.0]])]});}
            extrude(context, id + "F25", {"entities" : qUnion([Q0, Q1, Q2, Q3, Q4, Q5, Q6, Q7]), "operationType" : NewBodyOperationType.ADD, "depth" : 6.35 * mm});
        }
        {
            var Q0;
            {var subQ0=makeQuery(id+"F18.opExtrude","CAP_EDGE",EDGE,{"disambiguationData":[OSD([sQuery(id+"F17.wireOp",EDGE,"E69"),sQuery(id+"F17.wireOp",EDGE,"E74")])],"isStart":true});var subQ1=sQuery(id+"F23.wireOp",EDGE,"E84");var subQ4=makeQuery(id+"F23.imprint","INTERSECT",VERTEX,{"disambiguationData":[OD(0.0)],"derivedFrom":[subQ0,subQ1]});Q0=makeQuery(id+"F23.imprint","IMPRINT",FACE,{"disambiguationData":[TD([[makeQuery(id+"F23.imprint","IMPRINT",EDGE,{"disambiguationData":[TD([[subQ4,-1.0]])],"derivedFrom":subQ1}),1.0]])]});}
            var Q1;
            {var subQ5=sQuery(id+"F23.wireOp",EDGE,"E85");var subQ13=sQuery(id+"F23.wireOp",EDGE,"E87");var subQ15=makeQuery(id+"F23.imprint","INTERSECT",VERTEX,{"disambiguationData":[OD(0.0)],"derivedFrom":[subQ5,subQ13]});Q1=makeQuery(id+"F23.imprint","IMPRINT",FACE,{"disambiguationData":[TD([[makeQuery(id+"F23.imprint","IMPRINT",EDGE,{"disambiguationData":[TD([[subQ15,1.0]])],"derivedFrom":subQ5}),-1.0]])]});}
            var Q2;
            {var subQ5=sQuery(id+"F23.wireOp",EDGE,"E85");var subQ11=sQuery(id+"F23.wireOp",EDGE,"E86");var subQ13=makeQuery(id+"F23.imprint","INTERSECT",VERTEX,{"disambiguationData":[OD(0.0)],"derivedFrom":[subQ5,subQ11]});Q2=makeQuery(id+"F23.imprint","IMPRINT",FACE,{"disambiguationData":[TD([[makeQuery(id+"F23.imprint","IMPRINT",EDGE,{"disambiguationData":[TD([[subQ13,-1.0]])],"derivedFrom":subQ5}),-1.0]])]});}
            var Q3;
            {var subQ0=makeQuery(id+"F18.opExtrude","CAP_EDGE",EDGE,{"disambiguationData":[OSD([sQuery(id+"F17.wireOp",EDGE,"E69"),sQuery(id+"F17.wireOp",EDGE,"E74")])],"isStart":false});var subQ1=sQuery(id+"F23.wireOp",EDGE,"E84");var subQ4=makeQuery(id+"F23.imprint","INTERSECT",VERTEX,{"disambiguationData":[OD(0.0)],"derivedFrom":[subQ0,subQ1]});Q3=makeQuery(id+"F23.imprint","IMPRINT",FACE,{"disambiguationData":[TD([[makeQuery(id+"F23.imprint","IMPRINT",EDGE,{"disambiguationData":[TD([[subQ4,1.0]])],"derivedFrom":subQ1}),1.0]])]});}
            var Q4;
            {var subQ0=sQuery(id+"F23.wireOp",EDGE,"E87");Q4=makeQuery(id+"F23.imprint","IMPRINT",FACE,{"disambiguationData":[TD([[makeQuery(id+"F23.imprint","IMPRINT",EDGE,{"derivedFrom":subQ0}),-1.0]])]});}
            var Q5;
            {var subQ0=sQuery(id+"F23.wireOp",EDGE,"E86");Q5=makeQuery(id+"F23.imprint","IMPRINT",FACE,{"disambiguationData":[TD([[makeQuery(id+"F23.imprint","IMPRINT",EDGE,{"derivedFrom":subQ0}),1.0]])]});}
            extrude(context, id + "F26", {"entities" : qUnion([Q0, Q1, Q2, Q3, Q4, Q5]), "operationType" : NewBodyOperationType.ADD, "depth" : 19.43 * mm});
        }
        {
            var Q0;
            Q0=sQuery(id+"F23.wireOp",VERTEX,"E88.center");
            var Q1;
            Q1=qCreatedBy(makeId("Right.planeOp"),FACE);
            cPlane(context, id + "F27", {"entities" : qUnion([Q0, Q1]), "cplaneType" : CPlaneType.PLANE_POINT, "offset" : 152.4 * mm, "width" : 152.4 * mm, "height" : 152.4 * mm});
        }
        {
            var Q0;
            Q0=qCreatedBy(id+"F27.planeOp",FACE);
            var sketch = newSketch(context, id + "F28", { "sketchPlane" : qUnion([Q0])});
            skLineSegment(sketch, "E93.bottom", {"start": v(-6.11, 16.51) * mm, "end": v(-11.2, 16.51) * mm});
            skLineSegment(sketch, "E93.top", {"start": v(-6.11, 12.7) * mm, "end": v(-11.2, 12.7) * mm});
            skLineSegment(sketch, "E93.left", {"start": v(-6.11, 16.51) * mm, "end": v(-6.11, 12.7) * mm});
            skLineSegment(sketch, "E93.right", {"start": v(-11.2, 16.51) * mm, "end": v(-11.2, 12.7) * mm});
            skLineSegment(sketch, "E94.0", {"start": v(-16.27, 12.7) * mm, "end": v(-1.03, 12.7) * mm});
            skArc(sketch, "E95", {"start": v(-11.2, 16.51) * mm, "mid": v(-8.65, 19.05) * mm, "end": v(-6.11, 16.51) * mm});
            skSolve(sketch);
        }
        {
            var Q0;
            Q0=makeQuery(id+"F19.imprint","IMPRINT",FACE,{"disambiguationData":[TD([[makeQuery(id+"F19.imprint","IMPRINT",EDGE,{"derivedFrom":sQuery(id+"F19.wireOp",EDGE,"E77.0")}),-1.0]])]});
            var Q1;
            Q1=makeQuery(id+"F19.imprint","IMPRINT",FACE,{"disambiguationData":[TD([[makeQuery(id+"F19.imprint","IMPRINT",EDGE,{"derivedFrom":sQuery(id+"F19.wireOp",EDGE,"E83.2.MirrorCS")}),1.0]])]});
            extrude(context, id + "F29", {"entities" : qUnion([Q0, Q1]), "operationType" : NewBodyOperationType.REMOVE, "endBound" : BoundingType.THROUGH_ALL, "oppositeDirection" : true, "depth" : 25.4 * mm});
        }
        {
            var Q0;
            {var subQ0=sQuery(id+"F3.wireOp",EDGE,"E16");Q0=makeQuery(id+"F16.boolean.opBoolean","MERGE",FACE,{"derivedFrom":[makeQuery(id+"F5.boolean.opBoolean","MERGE",FACE,{"derivedFrom":[makeQuery(id+"F4.boolean.opBoolean","SPLIT",FACE,{"disambiguationData":[TD([makeQuery(id+"F1.opExtrude","SWEPT_FACE",FACE,{"disambiguationData":[OSD([sQuery(id+"F0.wireOp",EDGE,"E0.top")])]})])],"derivedFrom":makeQuery(id+"F4.opExtrude","SWEPT_FACE",FACE,{"disambiguationData":[OSD([subQ0])]})}),makeQuery(id+"F5.opExtrude","SWEPT_FACE",FACE,{"disambiguationData":[OSD([subQ0])]})]}),makeQuery(id+"F16.opExtrude","CAP_FACE",FACE,{"disambiguationData":[OSD([sQuery(id+"F15.wireOp",EDGE,"E44.0.5"),sQuery(id+"F15.wireOp",EDGE,"E45"),sQuery(id+"F15.wireOp",EDGE,"E46"),sQuery(id+"F15.wireOp",EDGE,"E47")])],"isStart":true})]});}
            var sketch = newSketch(context, id + "F30", { "sketchPlane" : qUnion([Q0])});
            skLineSegment(sketch, "E96.bottom", {"start": v(-69.85, 183.14) * mm, "end": v(-66.67, 183.14) * mm});
            skLineSegment(sketch, "E96.top", {"start": v(-69.85, 81.54) * mm, "end": v(-66.67, 81.54) * mm});
            skLineSegment(sketch, "E96.left", {"start": v(-69.85, 183.14) * mm, "end": v(-69.85, 81.54) * mm});
            skLineSegment(sketch, "E96.right", {"start": v(-66.67, 183.14) * mm, "end": v(-66.67, 81.54) * mm});
            skLineSegment(sketch, "E97.bottom", {"start": v(69.85, 183.14) * mm, "end": v(66.67, 183.14) * mm});
            skLineSegment(sketch, "E97.top", {"start": v(69.85, 81.54) * mm, "end": v(66.67, 81.54) * mm});
            skLineSegment(sketch, "E97.left", {"start": v(69.85, 183.14) * mm, "end": v(69.85, 81.54) * mm});
            skLineSegment(sketch, "E97.right", {"start": v(66.67, 183.14) * mm, "end": v(66.67, 81.54) * mm});
            skLineSegment(sketch, "E98", {"start": v(-66.67, 129.12) * mm, "end": v(-57.15, 183.14) * mm});
            skLineSegment(sketch, "E99", {"start": v(-57.15, 183.14) * mm, "end": v(-60.37, 183.14) * mm});
            skLineSegment(sketch, "E100", {"start": v(0, 103.56) * mm, "end": v(0, 192.4) * mm, "construction": true});
            skLineSegment(sketch, "E101", {"start": v(-66.67, 129.12) * mm, "end": v(-66.67, 147.4) * mm});
            skLineSegment(sketch, "E102", {"start": v(-66.67, 147.4) * mm, "end": v(-60.37, 183.14) * mm});
            skLineSegment(sketch, "E103.0.MirrorCS", {"start": v(66.67, 129.12) * mm, "end": v(57.15, 183.14) * mm});
            skLineSegment(sketch, "E104.0.MirrorCS", {"start": v(66.67, 147.4) * mm, "end": v(60.37, 183.14) * mm});
            skLineSegment(sketch, "E105.0.MirrorCS", {"start": v(66.67, 129.12) * mm, "end": v(66.67, 147.4) * mm});
            skLineSegment(sketch, "E106.0.MirrorCS", {"start": v(57.15, 183.14) * mm, "end": v(60.37, 183.14) * mm});
            skLineSegment(sketch, "E107.0", {"start": v(-69.85, 176.8) * mm, "end": v(-66.67, 176.8) * mm});
            skLineSegment(sketch, "E108.0", {"start": v(-69.85, 164.1) * mm, "end": v(-66.67, 164.1) * mm});
            skLineSegment(sketch, "E109.0", {"start": v(-69.85, 138.7) * mm, "end": v(-66.67, 138.7) * mm});
            skLineSegment(sketch, "E110.0", {"start": v(-69.85, 126) * mm, "end": v(-66.67, 126) * mm});
            skLineSegment(sketch, "E111.0", {"start": v(-69.85, 100.6) * mm, "end": v(-66.67, 100.6) * mm});
            skLineSegment(sketch, "E112.0", {"start": v(-69.85, 87.9) * mm, "end": v(-66.67, 87.9) * mm});
            skLineSegment(sketch, "E113.0", {"start": v(69.85, 87.9) * mm, "end": v(66.67, 87.9) * mm});
            skLineSegment(sketch, "E114.0", {"start": v(69.85, 100.6) * mm, "end": v(66.67, 100.6) * mm});
            skLineSegment(sketch, "E115.0", {"start": v(69.85, 126) * mm, "end": v(66.67, 126) * mm});
            skLineSegment(sketch, "E116.0", {"start": v(69.85, 138.7) * mm, "end": v(66.68, 138.7) * mm});
            skLineSegment(sketch, "E117.0", {"start": v(69.85, 164.1) * mm, "end": v(66.68, 164.1) * mm});
            skLineSegment(sketch, "E118.0", {"start": v(69.85, 176.8) * mm, "end": v(66.68, 176.8) * mm});
            skSolve(sketch);
        }
        {
            var Q0;
            {var subQ0=sQuery(id+"F30.wireOp",EDGE,"E107.0");var subQ1=makeQuery(id+"F30.imprint","IMPRINT",EDGE,{"derivedFrom":subQ0});var subQ4=sQuery(id+"F30.wireOp",EDGE,"E96.bottom");var subQ10=sQuery(id+"F30.wireOp",EDGE,"E96.top");var subQ17=sQuery(id+"F30.wireOp",EDGE,"E97.bottom");var subQ21=sQuery(id+"F30.wireOp",EDGE,"E113.0");var subQ22=makeQuery(id+"F30.imprint","IMPRINT",EDGE,{"derivedFrom":subQ21});var subQ23=sQuery(id+"F30.wireOp",EDGE,"E97.top");var subQ26=sQuery(id+"F30.wireOp",EDGE,"E108.0");var subQ27=makeQuery(id+"F30.imprint","IMPRINT",EDGE,{"derivedFrom":subQ26});var subQ30=sQuery(id+"F30.wireOp",EDGE,"E111.0");var subQ31=makeQuery(id+"F30.imprint","IMPRINT",EDGE,{"derivedFrom":subQ30});var subQ32=sQuery(id+"F30.wireOp",EDGE,"E110.0");var subQ33=makeQuery(id+"F30.imprint","IMPRINT",EDGE,{"derivedFrom":subQ32});var subQ38=sQuery(id+"F30.wireOp",EDGE,"E117.0");var subQ39=makeQuery(id+"F30.imprint","IMPRINT",EDGE,{"derivedFrom":subQ38});var subQ42=sQuery(id+"F30.wireOp",EDGE,"E115.0");var subQ43=makeQuery(id+"F30.imprint","IMPRINT",EDGE,{"derivedFrom":subQ42});var subQ44=sQuery(id+"F30.wireOp",EDGE,"E114.0");var subQ45=makeQuery(id+"F30.imprint","IMPRINT",EDGE,{"derivedFrom":subQ44});var subQ50=sQuery(id+"F30.wireOp",EDGE,"E109.0");var subQ51=makeQuery(id+"F30.imprint","IMPRINT",EDGE,{"derivedFrom":subQ50});var subQ53=sQuery(id+"F30.wireOp",EDGE,"E98");var subQ61=sQuery(id+"F30.wireOp",EDGE,"E116.0");var subQ62=makeQuery(id+"F30.imprint","IMPRINT",EDGE,{"derivedFrom":subQ61});var subQ69=sQuery(id+"F30.wireOp",EDGE,"E103.0.MirrorCS");Q0=qUnion([makeQuery(id+"F30.imprint","IMPRINT",FACE,{"disambiguationData":[TD([[makeQuery(id+"F30.imprint","IMPRINT",EDGE,{"derivedFrom":subQ4}),-1.0]])]}),makeQuery(id+"F30.imprint","IMPRINT",FACE,{"disambiguationData":[TD([[makeQuery(id+"F30.imprint","IMPRINT",EDGE,{"derivedFrom":subQ10}),1.0]])]}),makeQuery(id+"F30.imprint","IMPRINT",FACE,{"disambiguationData":[TD([[makeQuery(id+"F30.imprint","IMPRINT",EDGE,{"derivedFrom":subQ17}),-1.0]])]}),makeQuery(id+"F30.imprint","IMPRINT",FACE,{"disambiguationData":[TD([[makeQuery(id+"F30.imprint","IMPRINT",EDGE,{"derivedFrom":subQ23}),-1.0]])]}),makeQuery(id+"F30.imprint","IMPRINT",FACE,{"disambiguationData":[TD([[subQ1,-1.0]])]}),makeQuery(id+"F30.imprint","IMPRINT",FACE,{"disambiguationData":[TD([[subQ33,-1.0]])]}),makeQuery(id+"F30.imprint","IMPRINT",FACE,{"disambiguationData":[TD([[subQ31,-1.0]])]}),makeQuery(id+"F30.imprint","IMPRINT",FACE,{"disambiguationData":[TD([[subQ39,-1.0]])]}),makeQuery(id+"F30.imprint","IMPRINT",FACE,{"disambiguationData":[TD([[subQ45,-1.0]])]}),makeQuery(id+"F30.imprint","IMPRINT",FACE,{"disambiguationData":[TD([[subQ22,-1.0]])]}),makeQuery(id+"F30.imprint","IMPRINT",FACE,{"disambiguationData":[TD([[subQ51,-1.0]])]}),makeQuery(id+"F30.imprint","IMPRINT",FACE,{"disambiguationData":[TD([[subQ27,-1.0]])]}),makeQuery(id+"F30.imprint","IMPRINT",FACE,{"disambiguationData":[TD([[subQ62,-1.0]])]}),makeQuery(id+"F30.imprint","IMPRINT",FACE,{"disambiguationData":[TD([[subQ43,-1.0]])]}),makeQuery(id+"F30.imprint","IMPRINT",FACE,{"disambiguationData":[TD([[makeQuery(id+"F30.imprint","IMPRINT",EDGE,{"derivedFrom":subQ53}),1.0]])]}),makeQuery(id+"F30.imprint","IMPRINT",FACE,{"disambiguationData":[TD([[makeQuery(id+"F30.imprint","IMPRINT",EDGE,{"derivedFrom":subQ69}),-1.0]])]})]);}
            extrude(context, id + "F31", {"entities" : qUnion([Q0]), "depth" : 25.4 * mm});
        }
        {
            var Q0;
            {var subQ1=sQuery(id+"F30.wireOp",EDGE,"E109.0");Q0=makeQuery(id+"F30.imprint","IMPRINT",FACE,{"disambiguationData":[TD([[makeQuery(id+"F30.imprint","IMPRINT",EDGE,{"derivedFrom":subQ1}),-1.0]])]});}
            var Q1;
            {var subQ1=sQuery(id+"F30.wireOp",EDGE,"E107.0");Q1=makeQuery(id+"F30.imprint","IMPRINT",FACE,{"disambiguationData":[TD([[makeQuery(id+"F30.imprint","IMPRINT",EDGE,{"derivedFrom":subQ1}),-1.0]])]});}
            var Q2;
            {var subQ1=sQuery(id+"F30.wireOp",EDGE,"E111.0");Q2=makeQuery(id+"F30.imprint","IMPRINT",FACE,{"disambiguationData":[TD([[makeQuery(id+"F30.imprint","IMPRINT",EDGE,{"derivedFrom":subQ1}),-1.0]])]});}
            var Q3;
            Q3=makeQuery(id+"F16.opExtrude","CAP_FACE",FACE,{"disambiguationData":[OSD([sQuery(id+"F15.wireOp",EDGE,"E44.0.5"),sQuery(id+"F15.wireOp",EDGE,"E45"),sQuery(id+"F15.wireOp",EDGE,"E46"),sQuery(id+"F15.wireOp",EDGE,"E47"),sQuery(id+"F15.wireOp",EDGE,"E48.bottom"),sQuery(id+"F15.wireOp",EDGE,"E48.top"),sQuery(id+"F15.wireOp",EDGE,"E48.left"),sQuery(id+"F15.wireOp",EDGE,"E48.right"),sQuery(id+"F15.wireOp",EDGE,"E49.1.0.0"),sQuery(id+"F15.wireOp",EDGE,"E49.1.0.1"),sQuery(id+"F15.wireOp",EDGE,"E49.1.0.2"),sQuery(id+"F15.wireOp",EDGE,"E49.1.0.3"),sQuery(id+"F15.wireOp",EDGE,"E49.2.0.0"),sQuery(id+"F15.wireOp",EDGE,"E49.2.0.1"),sQuery(id+"F15.wireOp",EDGE,"E49.2.0.2"),sQuery(id+"F15.wireOp",EDGE,"E49.2.0.3"),sQuery(id+"F15.wireOp",EDGE,"E50.0.3.0"),sQuery(id+"F15.wireOp",EDGE,"E50.3.3.0"),sQuery(id+"F15.wireOp",EDGE,"E50.6.3.0"),sQuery(id+"F15.wireOp",EDGE,"E50.9.3.0"),sQuery(id+"F15.wireOp",EDGE,"E51.0.4.0"),sQuery(id+"F15.wireOp",EDGE,"E51.3.4.0"),sQuery(id+"F15.wireOp",EDGE,"E51.6.4.0"),sQuery(id+"F15.wireOp",EDGE,"E51.9.4.0"),sQuery(id+"F15.wireOp",EDGE,"E52.bottom"),sQuery(id+"F15.wireOp",EDGE,"E52.top"),sQuery(id+"F15.wireOp",EDGE,"E52.right"),sQuery(id+"F15.wireOp",EDGE,"E54.1.0.0"),sQuery(id+"F15.wireOp",EDGE,"E54.1.0.1"),sQuery(id+"F15.wireOp",EDGE,"E54.1.0.2"),sQuery(id+"F15.wireOp",EDGE,"E54.2.0.0"),sQuery(id+"F15.wireOp",EDGE,"E54.2.0.1"),sQuery(id+"F15.wireOp",EDGE,"E54.2.0.2"),sQuery(id+"F15.wireOp",EDGE,"E55.0.MirrorCS"),sQuery(id+"F15.wireOp",EDGE,"E56.0.MirrorCS"),sQuery(id+"F15.wireOp",EDGE,"E57.0.MirrorCS"),sQuery(id+"F15.wireOp",EDGE,"E58.0.MirrorCS"),sQuery(id+"F15.wireOp",EDGE,"E59.0.MirrorCS"),sQuery(id+"F15.wireOp",EDGE,"E60.0.MirrorCS"),sQuery(id+"F15.wireOp",EDGE,"E61.0.MirrorCS"),sQuery(id+"F15.wireOp",EDGE,"E62.0.MirrorCS"),sQuery(id+"F15.wireOp",EDGE,"E63.0.MirrorCS")])],"isStart":false});
            extrude(context, id + "F32", {"entities" : qUnion([Q0, Q1, Q2]), "operationType" : NewBodyOperationType.ADD, "endBound" : BoundingType.UP_TO_SURFACE, "oppositeDirection" : true, "endBoundEntityFace" : qUnion([Q3]), "depth" : 25.4 * mm});
        }
        {
            var Q0;
            {var subQ1=sQuery(id+"F30.wireOp",EDGE,"E117.0");Q0=makeQuery(id+"F30.imprint","IMPRINT",FACE,{"disambiguationData":[TD([[makeQuery(id+"F30.imprint","IMPRINT",EDGE,{"derivedFrom":subQ1}),-1.0]])]});}
            var Q1;
            {var subQ1=sQuery(id+"F30.wireOp",EDGE,"E115.0");Q1=makeQuery(id+"F30.imprint","IMPRINT",FACE,{"disambiguationData":[TD([[makeQuery(id+"F30.imprint","IMPRINT",EDGE,{"derivedFrom":subQ1}),-1.0]])]});}
            var Q2;
            {var subQ1=sQuery(id+"F30.wireOp",EDGE,"E113.0");Q2=makeQuery(id+"F30.imprint","IMPRINT",FACE,{"disambiguationData":[TD([[makeQuery(id+"F30.imprint","IMPRINT",EDGE,{"derivedFrom":subQ1}),-1.0]])]});}
            var Q3;
            Q3=makeQuery(id+"F16.opExtrude","CAP_FACE",FACE,{"disambiguationData":[OSD([sQuery(id+"F15.wireOp",EDGE,"E44.0.5"),sQuery(id+"F15.wireOp",EDGE,"E45"),sQuery(id+"F15.wireOp",EDGE,"E46"),sQuery(id+"F15.wireOp",EDGE,"E47"),sQuery(id+"F15.wireOp",EDGE,"E48.bottom"),sQuery(id+"F15.wireOp",EDGE,"E48.top"),sQuery(id+"F15.wireOp",EDGE,"E48.left"),sQuery(id+"F15.wireOp",EDGE,"E48.right"),sQuery(id+"F15.wireOp",EDGE,"E49.1.0.0"),sQuery(id+"F15.wireOp",EDGE,"E49.1.0.1"),sQuery(id+"F15.wireOp",EDGE,"E49.1.0.2"),sQuery(id+"F15.wireOp",EDGE,"E49.1.0.3"),sQuery(id+"F15.wireOp",EDGE,"E49.2.0.0"),sQuery(id+"F15.wireOp",EDGE,"E49.2.0.1"),sQuery(id+"F15.wireOp",EDGE,"E49.2.0.2"),sQuery(id+"F15.wireOp",EDGE,"E49.2.0.3"),sQuery(id+"F15.wireOp",EDGE,"E50.0.3.0"),sQuery(id+"F15.wireOp",EDGE,"E50.3.3.0"),sQuery(id+"F15.wireOp",EDGE,"E50.6.3.0"),sQuery(id+"F15.wireOp",EDGE,"E50.9.3.0"),sQuery(id+"F15.wireOp",EDGE,"E51.0.4.0"),sQuery(id+"F15.wireOp",EDGE,"E51.3.4.0"),sQuery(id+"F15.wireOp",EDGE,"E51.6.4.0"),sQuery(id+"F15.wireOp",EDGE,"E51.9.4.0"),sQuery(id+"F15.wireOp",EDGE,"E52.bottom"),sQuery(id+"F15.wireOp",EDGE,"E52.top"),sQuery(id+"F15.wireOp",EDGE,"E52.right"),sQuery(id+"F15.wireOp",EDGE,"E54.1.0.0"),sQuery(id+"F15.wireOp",EDGE,"E54.1.0.1"),sQuery(id+"F15.wireOp",EDGE,"E54.1.0.2"),sQuery(id+"F15.wireOp",EDGE,"E54.2.0.0"),sQuery(id+"F15.wireOp",EDGE,"E54.2.0.1"),sQuery(id+"F15.wireOp",EDGE,"E54.2.0.2"),sQuery(id+"F15.wireOp",EDGE,"E55.0.MirrorCS"),sQuery(id+"F15.wireOp",EDGE,"E56.0.MirrorCS"),sQuery(id+"F15.wireOp",EDGE,"E57.0.MirrorCS"),sQuery(id+"F15.wireOp",EDGE,"E58.0.MirrorCS"),sQuery(id+"F15.wireOp",EDGE,"E59.0.MirrorCS"),sQuery(id+"F15.wireOp",EDGE,"E60.0.MirrorCS"),sQuery(id+"F15.wireOp",EDGE,"E61.0.MirrorCS"),sQuery(id+"F15.wireOp",EDGE,"E62.0.MirrorCS"),sQuery(id+"F15.wireOp",EDGE,"E63.0.MirrorCS")])],"isStart":false});
            extrude(context, id + "F33", {"entities" : qUnion([Q0, Q1, Q2]), "operationType" : NewBodyOperationType.ADD, "endBound" : BoundingType.UP_TO_SURFACE, "oppositeDirection" : true, "endBoundEntityFace" : qUnion([Q3]), "depth" : 25.4 * mm});
        }
        {
            var Q0;
            Q0=makeQuery(id+"F18.opExtrude","SWEPT_BODY",BODY,{"disambiguationData":[OSD([sQuery(id+"F17.wireOp",EDGE,"E65.top"),sQuery(id+"F17.wireOp",EDGE,"E65.left"),sQuery(id+"F17.wireOp",EDGE,"E67"),sQuery(id+"F17.wireOp",EDGE,"E69"),sQuery(id+"F17.wireOp",EDGE,"E70"),sQuery(id+"F17.wireOp",EDGE,"E71"),sQuery(id+"F17.wireOp",EDGE,"E72")])]});
            var Q1;
            Q1=qCreatedBy(makeId("Right.planeOp"),FACE);
            mirror(context, id + "F34", {"entities" : qUnion([Q0]), "mirrorPlane" : qUnion([Q1])});
        }
        {
            var Q0;
            Q0=qCreatedBy(makeId("Right.planeOp"),FACE);
            var sketch = newSketch(context, id + "F35", { "sketchPlane" : qUnion([Q0])});
            skArc(sketch, "E119", {"start": v(-21.15, 0) * mm, "mid": v(-33.85, 12.7) * mm, "end": v(-46.55, 0) * mm});
            skLineSegment(sketch, "E120", {"start": v(-21.15, 0) * mm, "end": v(-46.55, 0) * mm});
            skSolve(sketch);
        }
        {
            var Q0;
            Q0=makeQuery(id+"F35.imprint","IMPRINT",FACE,{"disambiguationData":[TD([[makeQuery(id+"F35.imprint","IMPRINT",EDGE,{"derivedFrom":sQuery(id+"F35.wireOp",EDGE,"E119")}),1.0]])]});
            extrude(context, id + "F36", {"entities" : qUnion([Q0]), "endBound" : BoundingType.SYMMETRIC, "depth" : 158.42 * mm});
        }
        {
            var Q0;
            Q0=qCreatedBy(makeId("Front.planeOp"),FACE);
            cPlane(context, id + "F37", {"entities" : qUnion([Q0]), "cplaneType" : CPlaneType.OFFSET, "offset" : 25.4 * mm, "oppositeDirection" : true, "width" : 152.4 * mm, "height" : 152.4 * mm});
        }
        {
            var Q0;
            {var subQ3=makeQuery(id+"F28.imprint","IMPRINT",EDGE,{"derivedFrom":sQuery(id+"F28.wireOp",EDGE,"E93.bottom")});Q0=qUnion([makeQuery(id+"F28.imprint","IMPRINT",FACE,{"disambiguationData":[TD([[subQ3,1.0]])]}),makeQuery(id+"F28.imprint","IMPRINT",FACE,{"disambiguationData":[TD([[subQ3,-1.0]])]})]);}
            extrude(context, id + "F38", {"entities" : qUnion([Q0]), "operationType" : NewBodyOperationType.REMOVE, "endBound" : BoundingType.SYMMETRIC, "oppositeDirection" : true, "depth" : 25.4 * mm});
        }
    });
